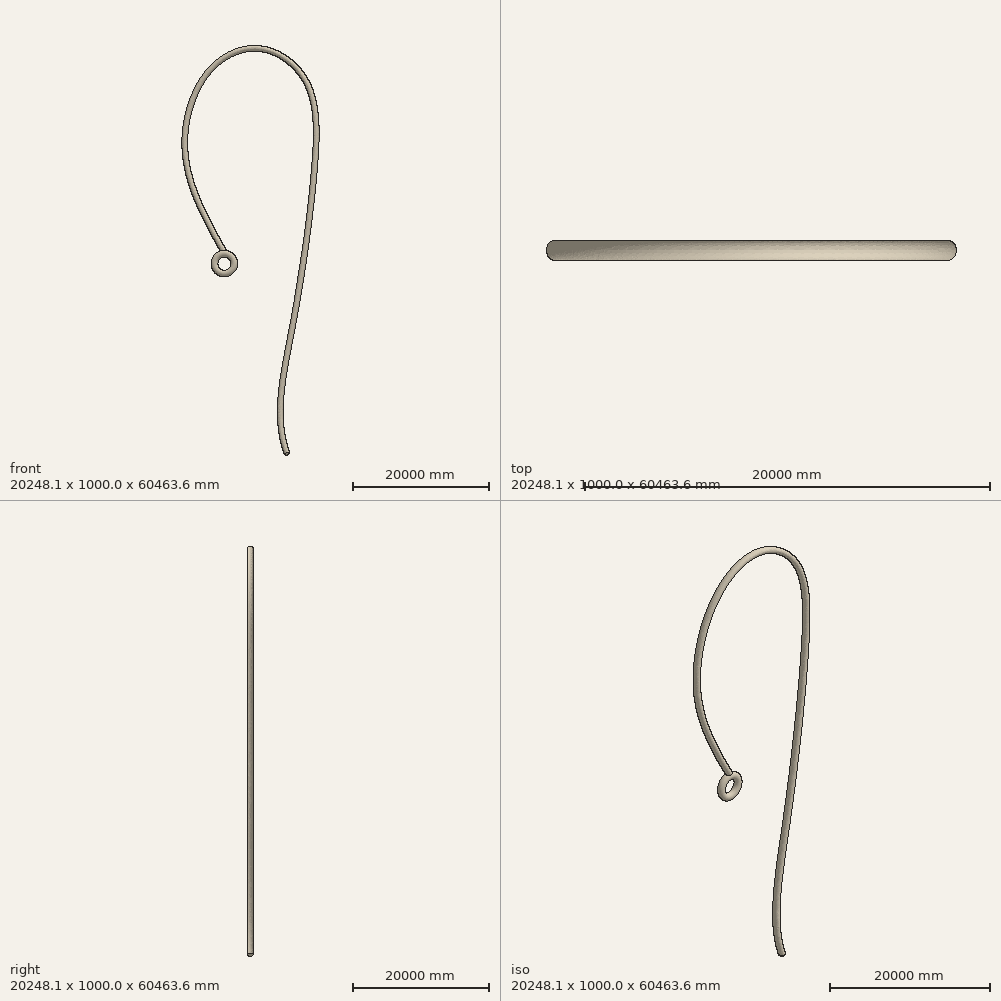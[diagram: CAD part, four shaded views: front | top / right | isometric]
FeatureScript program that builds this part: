
annotation { "Feature Type Name" : "Feature", "Feature Type Description" : "" }
export const myFeature = defineFeature(function(context is Context, id is Id, definition is map)
    precondition{}
    {
        {
            var Q0;
            Q0=qCreatedBy(makeId("Front.planeOp"),FACE);
            var sketch = newSketch(context, id + "F0", { "sketchPlane" : qUnion([Q0])});
            skFitSpline(sketch, "E0", {"points": [v(6369.2, -30193.95) * mm, v(6955.64, -11606.44) * mm, v(10270.89, 12118.15) * mm, v(8989.12, 25054.07) * mm, v(2336.76, 29806.05) * mm, v(-4445.8, 27307.94) * mm, v(-8442.96, 19670.37) * mm, v(-7375.59, 8512.77) * mm, v(-3124.1, 0) * mm], "startDerivative": vector(-42768.63, 105530.32) * mm, "endDerivative": vector(79.66, -132.73) * mm});
            skSolve(sketch);
        }
        {
            var Q0;
            Q0=qCreatedBy(makeId("Top.planeOp"),FACE);
            var sketch = newSketch(context, id + "F1", { "sketchPlane" : qUnion([Q0])});
            skCircle(sketch, "E1", {"center": v(-3124.1, 0) * mm, "radius": 500 * mm});
            skSolve(sketch);
        }
        {
            var Q0;
            Q0=makeQuery(id+"F1.imprint","IMPRINT",FACE,{"disambiguationData":[TD([[makeQuery(id+"F1.imprint","IMPRINT",EDGE,{"derivedFrom":sQuery(id+"F1.wireOp",EDGE,"E1")}),1.0]])]});
            var Q1;
            Q1=sQuery(id+"F0.wireOp",EDGE,"E0");
            sweep(context, id + "F2", {"profiles" : qUnion([Q0]), "path" : qUnion([Q1])});
        }
        {
            var Q0;
            Q0=makeQuery(id+"F2.opSweep","CAP_EDGE",EDGE,{"disambiguationData":[OSD([sQuery(id+"F0.wireOp",VERTEX,"E0.start"),sQuery(id+"F1.wireOp",EDGE,"E1")])],"isStart":false});
            fillet(context, id + "F3", {"entities" : qUnion([Q0]), "radius" : 384.23 * mm, "tangentPropagation" : true, "allowEdgeOverflow" : false});
        }
        {
            var Q0;
            Q0=qCreatedBy(makeId("Right.planeOp"),FACE);
            cPlane(context, id + "F4", {"entities" : qUnion([Q0]), "cplaneType" : CPlaneType.OFFSET, "offset" : 3000 * mm, "oppositeDirection" : true, "width" : 150 * mm, "height" : 150 * mm});
        }
        {
            var Q0;
            Q0=qCreatedBy(id+"F4.planeOp",FACE);
            var sketch = newSketch(context, id + "F5", { "sketchPlane" : qUnion([Q0])});
            skCircle(sketch, "E2", {"center": v(0, -3348.35) * mm, "radius": 500 * mm});
            skLineSegment(sketch, "E3", {"start": v(4227.82, -1889.03) * mm, "end": v(-5465.34, -1889.03) * mm, "construction": true});
            skSolve(sketch);
        }
        {
            var Q0;
            Q0 = qSketchRegion(id + "F5", true);
            var Q1;
            Q1=sQuery(id+"F5.wireOp",EDGE,"E3");
            revolve(context, id + "F6", {"operationType" : NewBodyOperationType.ADD, "entities" : qUnion([Q0]), "axis" : qUnion([Q1]), "revolveType" : RevolveType.FULL});
        }
    });
